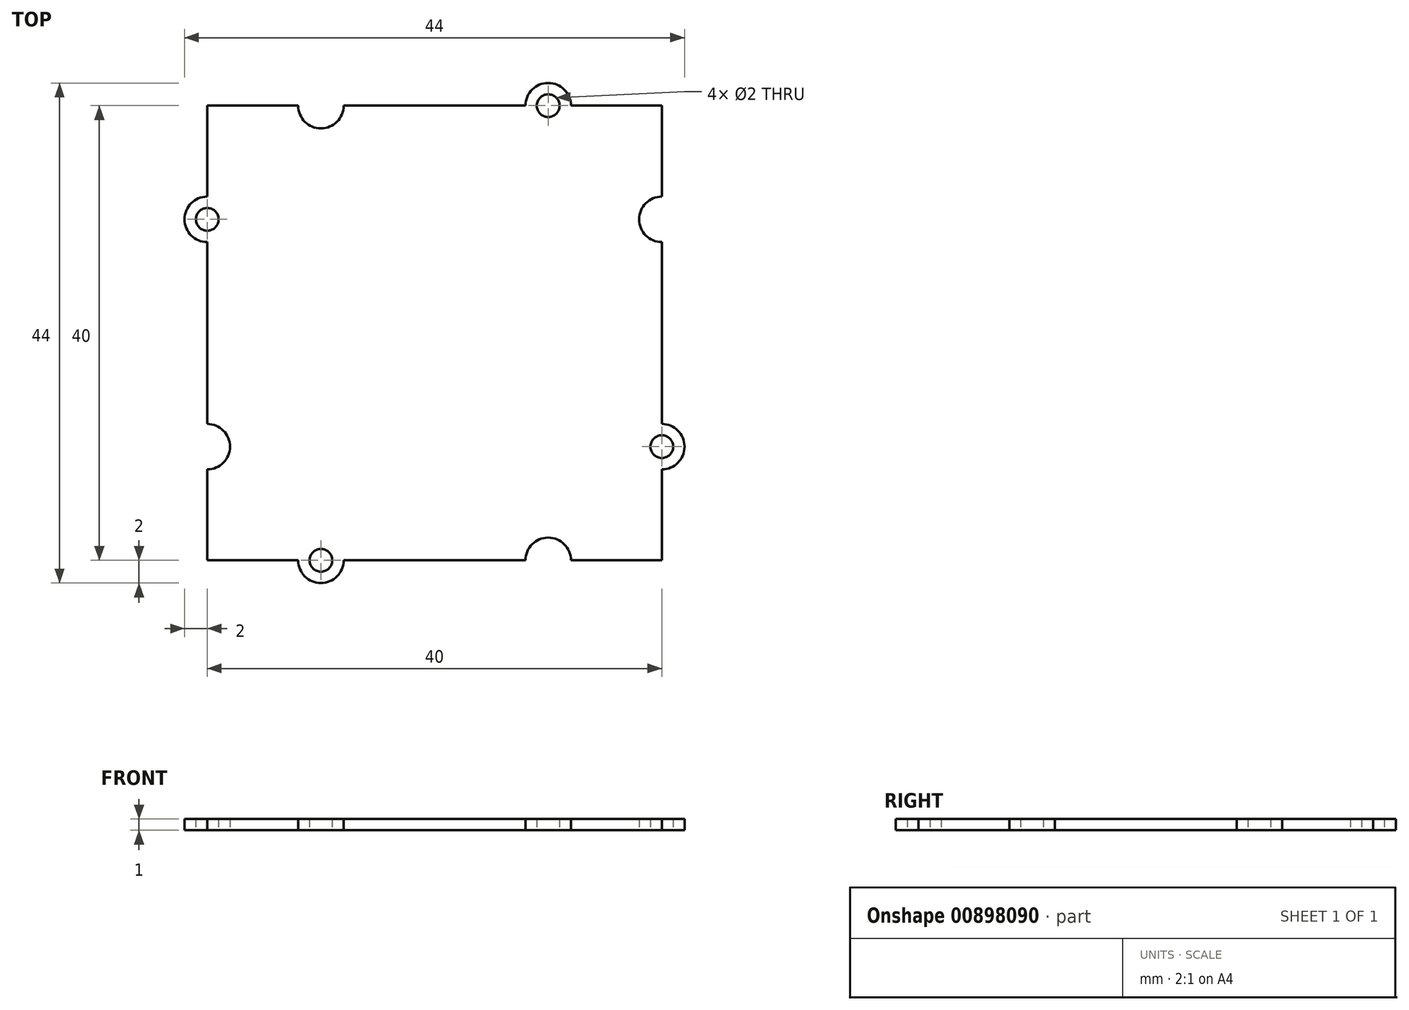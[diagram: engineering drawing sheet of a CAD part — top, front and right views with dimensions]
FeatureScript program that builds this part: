
annotation { "Feature Type Name" : "Feature", "Feature Type Description" : "" }
export const myFeature = defineFeature(function(context is Context, id is Id, definition is map)
    precondition{}
    {
        {
            var Q0;
            Q0=qCreatedBy(makeId("Top.planeOp"),FACE);
            var sketch = newSketch(context, id + "F0", { "sketchPlane" : qUnion([Q0])});
            skLineSegment(sketch, "E0.bottom", {"start": v(20, 20) * mm, "end": v(-20, 20) * mm});
            skLineSegment(sketch, "E0.top", {"start": v(20, -20) * mm, "end": v(-20, -20) * mm});
            skLineSegment(sketch, "E0.left", {"start": v(20, 20) * mm, "end": v(20, -20) * mm});
            skLineSegment(sketch, "E0.right", {"start": v(-20, 20) * mm, "end": v(-20, -20) * mm});
            skPoint(sketch, "E0.middle", {"position": v(0, 0) * mm});
            skPoint(sketch, "E1", {"position": v(20, -10) * mm});
            skPoint(sketch, "E2", {"position": v(10, 20) * mm});
            skPoint(sketch, "E3", {"position": v(-20, 10) * mm});
            skPoint(sketch, "E4", {"position": v(-10, -20) * mm});
            skPoint(sketch, "E5", {"position": v(20, 10) * mm});
            skPoint(sketch, "E6", {"position": v(-20, -10) * mm});
            skPoint(sketch, "E7", {"position": v(-10, 20) * mm});
            skPoint(sketch, "E8", {"position": v(10, -20) * mm});
            skArc(sketch, "E9", {"start": v(8, 20) * mm, "mid": v(10, 22) * mm, "end": v(12, 20) * mm});
            skArc(sketch, "E10", {"start": v(20, -12) * mm, "mid": v(22, -10) * mm, "end": v(20, -8) * mm});
            skArc(sketch, "E11", {"start": v(-12, -20) * mm, "mid": v(-10, -22) * mm, "end": v(-8, -20) * mm});
            skArc(sketch, "E12", {"start": v(-20, 12) * mm, "mid": v(-22, 10) * mm, "end": v(-20, 8) * mm});
            skCircle(sketch, "E13", {"center": v(-20, -10) * mm, "radius": 2 * mm});
            skCircle(sketch, "E14", {"center": v(10, -20) * mm, "radius": 2 * mm});
            skCircle(sketch, "E15", {"center": v(20, 10) * mm, "radius": 2 * mm});
            skCircle(sketch, "E16", {"center": v(-10, 20) * mm, "radius": 2 * mm});
            skSolve(sketch);
        }
        {
            var Q0;
            Q0 = qSketchRegion(id + "F0", true);
            extrude(context, id + "F1", {"entities" : qUnion([Q0]), "depth" : 1 * mm, "offsetDistance" : 25 * mm});
        }
        {
            var Q0;
            Q0=sQuery(id+"F0.wireOp",VERTEX,"E6");
            var Q1;
            Q1=sQuery(id+"F0.wireOp",VERTEX,"E7");
            var Q2;
            Q2=sQuery(id+"F0.wireOp",VERTEX,"E5");
            var Q3;
            Q3=sQuery(id+"F0.wireOp",VERTEX,"E8");
            var Q4;
            Q4=makeQuery(id+"F1.opExtrude","SWEPT_BODY",BODY,{"disambiguationData":[OSD([sQuery(id+"F0.wireOp",EDGE,"E0.bottom"),sQuery(id+"F0.wireOp",EDGE,"E0.top"),sQuery(id+"F0.wireOp",EDGE,"E0.left"),sQuery(id+"F0.wireOp",EDGE,"E0.right"),sQuery(id+"F0.wireOp",EDGE,"E9"),sQuery(id+"F0.wireOp",EDGE,"E10"),sQuery(id+"F0.wireOp",EDGE,"E11"),sQuery(id+"F0.wireOp",EDGE,"E12"),sQuery(id+"F0.wireOp",EDGE,"E13"),sQuery(id+"F0.wireOp",EDGE,"E14"),sQuery(id+"F0.wireOp",EDGE,"E15"),sQuery(id+"F0.wireOp",EDGE,"E16")])]});
            hole(context, id + "F2", {"style" : HoleStyle.SIMPLE, "endStyle" : HoleEndStyle.THROUGH, "oppositeDirection" : true, "holeDiameter" : 4 * mm, "majorDiameter" : 5 * mm, "tappedDepth" : 12 * mm, "tapClearance" : 3, "locations" : qUnion([Q0, Q1, Q2, Q3]), "scope" : qUnion([Q4])});
        }
        {
            var Q0;
            Q0=sQuery(id+"F0.wireOp",VERTEX,"E2");
            var Q1;
            Q1=sQuery(id+"F0.wireOp",VERTEX,"E3");
            var Q2;
            Q2=sQuery(id+"F0.wireOp",VERTEX,"E4");
            var Q3;
            Q3=sQuery(id+"F0.wireOp",VERTEX,"E1");
            var Q4;
            Q4=makeQuery(id+"F1.opExtrude","SWEPT_BODY",BODY,{"disambiguationData":[OSD([sQuery(id+"F0.wireOp",EDGE,"E0.bottom"),sQuery(id+"F0.wireOp",EDGE,"E0.top"),sQuery(id+"F0.wireOp",EDGE,"E0.left"),sQuery(id+"F0.wireOp",EDGE,"E0.right"),sQuery(id+"F0.wireOp",EDGE,"E9"),sQuery(id+"F0.wireOp",EDGE,"E10"),sQuery(id+"F0.wireOp",EDGE,"E11"),sQuery(id+"F0.wireOp",EDGE,"E12"),sQuery(id+"F0.wireOp",EDGE,"E13"),sQuery(id+"F0.wireOp",EDGE,"E14"),sQuery(id+"F0.wireOp",EDGE,"E15"),sQuery(id+"F0.wireOp",EDGE,"E16")])]});
            hole(context, id + "F3", {"style" : HoleStyle.SIMPLE, "endStyle" : HoleEndStyle.THROUGH, "oppositeDirection" : true, "holeDiameter" : 2 * mm, "majorDiameter" : 5 * mm, "tappedDepth" : 12 * mm, "tapClearance" : 3, "locations" : qUnion([Q0, Q1, Q2, Q3]), "scope" : qUnion([Q4])});
        }
    });
